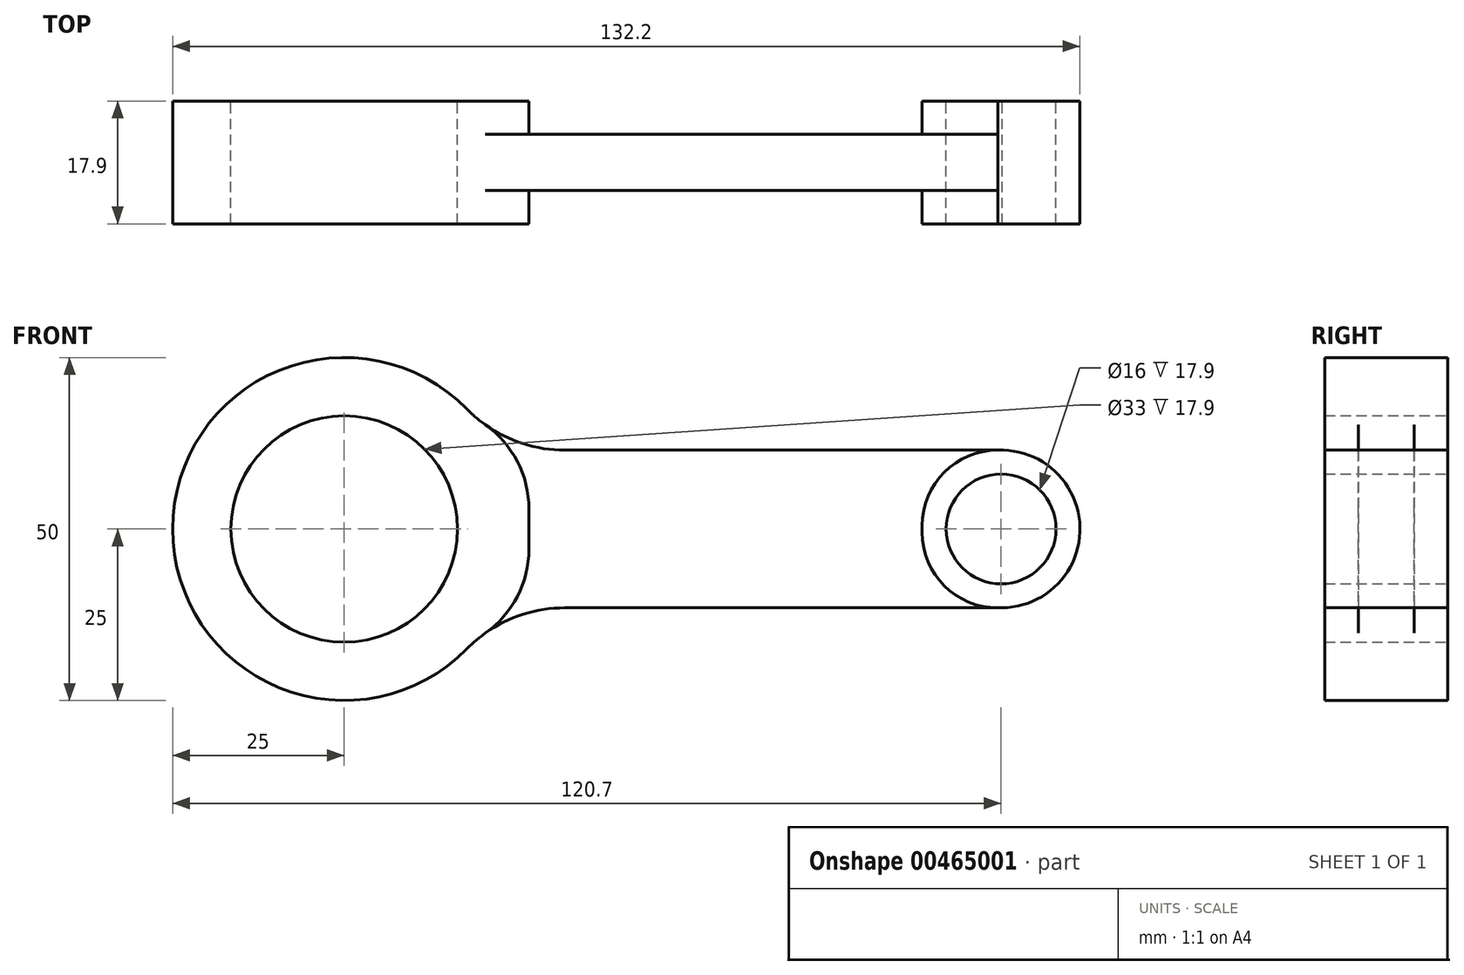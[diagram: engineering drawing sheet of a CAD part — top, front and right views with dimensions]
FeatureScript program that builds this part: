
annotation { "Feature Type Name" : "Feature", "Feature Type Description" : "" }
export const myFeature = defineFeature(function(context is Context, id is Id, definition is map)
    precondition{}
    {
        {
            var Q0;
            Q0=qCreatedBy(makeId("Front.planeOp"),FACE);
            var sketch = newSketch(context, id + "F0", { "sketchPlane" : qUnion([Q0])});
            skCircle(sketch, "E0", {"center": v(0, 0) * mm, "radius": 16.5 * mm});
            skCircle(sketch, "E1", {"center": v(95.7, 0) * mm, "radius": 8 * mm});
            skArc(sketch, "E2", {"start": v(95.55, -11.5) * mm, "mid": v(107.2, 0.15) * mm, "end": v(95.26, 11.5) * mm});
            skArc(sketch, "E3", {"start": v(17.86, 17.5) * mm, "mid": v(-25, 0) * mm, "end": v(17.85, -17.5) * mm});
            skLineSegment(sketch, "E4", {"start": v(95.26, 11.5) * mm, "end": v(32.14, 11.5) * mm});
            skLineSegment(sketch, "E5", {"start": v(95.85, -11.5) * mm, "end": v(32.14, -11.5) * mm});
            skPoint(sketch, "E6.visualSharp", {"position": v(22.2, 11.5) * mm});
            skArc(sketch, "E6.filletArc", {"start": v(17.86, 17.5) * mm, "mid": v(24.4, 13.05) * mm, "end": v(32.14, 11.5) * mm});
            skPoint(sketch, "E7.visualSharp", {"position": v(22.2, -11.5) * mm});
            skArc(sketch, "E7.filletArc", {"start": v(32.14, -11.5) * mm, "mid": v(24.4, -13.06) * mm, "end": v(17.85, -17.5) * mm});
            skSolve(sketch);
        }
        {
            var Q0;
            Q0=makeQuery(id+"F0.imprint","IMPRINT",FACE,{"disambiguationData":[TD([[makeQuery(id+"F0.imprint","IMPRINT",EDGE,{"derivedFrom":sQuery(id+"F0.wireOp",EDGE,"E0")}),-1.0]])]});
            extrude(context, id + "F1", {"entities" : qUnion([Q0]), "depth" : 17.9 * mm});
        }
        {
            var Q0;
            Q0=qCreatedBy(makeId("Top.planeOp"),FACE);
            var sketch = newSketch(context, id + "F2", { "sketchPlane" : qUnion([Q0])});
            skLineSegment(sketch, "E8", {"start": v(-25, -17.9) * mm, "end": v(-25, 0) * mm, "construction": true});
            skLineSegment(sketch, "E9", {"start": v(107.2, 0) * mm, "end": v(107.2, -17.9) * mm, "construction": true});
            skLineSegment(sketch, "E10", {"start": v(-25, -8.95) * mm, "end": v(107.2, -8.95) * mm, "construction": true});
            skLineSegment(sketch, "E11.bottom", {"start": v(26.9, 6.17) * mm, "end": v(84.2, 6.17) * mm});
            skLineSegment(sketch, "E11.top", {"start": v(26.9, -4.88) * mm, "end": v(84.2, -4.88) * mm});
            skLineSegment(sketch, "E11.left", {"start": v(26.9, 6.17) * mm, "end": v(26.9, -4.88) * mm});
            skLineSegment(sketch, "E11.right", {"start": v(84.2, 6.17) * mm, "end": v(84.2, -4.88) * mm});
            skLineSegment(sketch, "E12.bottom", {"start": v(26.9, -23.79) * mm, "end": v(84.2, -23.79) * mm});
            skLineSegment(sketch, "E12.top", {"start": v(26.9, -13.03) * mm, "end": v(84.2, -13.03) * mm});
            skLineSegment(sketch, "E12.left", {"start": v(26.9, -23.79) * mm, "end": v(26.9, -13.03) * mm});
            skLineSegment(sketch, "E12.right", {"start": v(84.2, -23.79) * mm, "end": v(84.2, -13.03) * mm});
            skSolve(sketch);
        }
        {
            var Q0;
            Q0 = qSketchRegion(id + "F2", true);
            extrude(context, id + "F3", {"entities" : qUnion([Q0]), "operationType" : NewBodyOperationType.REMOVE, "endBound" : BoundingType.THROUGH_ALL, "oppositeDirection" : true, "depth" : 25 * mm, "hasSecondDirection" : true, "secondDirectionBound" : SecondDirectionBoundingType.THROUGH_ALL, "secondDirectionOppositeDirection" : false, "secondDirectionDepth" : 25 * mm});
        }
        {
            var Q0;
            Q0=makeQuery(id+"F3.boolean.opBoolean","INTERSECT",EDGE,{"derivedFrom":[makeQuery(id+"F1.opExtrude","SWEPT_FACE",FACE,{"disambiguationData":[OSD([sQuery(id+"F0.wireOp",EDGE,"E5")])]}),makeQuery(id+"F3.opExtrude","SWEPT_FACE",FACE,{"disambiguationData":[OSD([sQuery(id+"F2.wireOp",EDGE,"E11.right")])]})]});
            fillet(context, id + "F4", {"entities" : qUnion([Q0]), "radius" : 11 * mm, "tangentPropagation" : true, "allowEdgeOverflow" : false});
        }
        {
            var Q0;
            Q0=makeQuery(id+"F3.boolean.opBoolean","INTERSECT",EDGE,{"derivedFrom":[makeQuery(id+"F1.opExtrude","SWEPT_FACE",FACE,{"disambiguationData":[OSD([sQuery(id+"F0.wireOp",EDGE,"E4")])]}),makeQuery(id+"F3.opExtrude","SWEPT_FACE",FACE,{"disambiguationData":[OSD([sQuery(id+"F2.wireOp",EDGE,"E11.right")])]})]});
            fillet(context, id + "F5", {"entities" : qUnion([Q0]), "radius" : 11 * mm, "tangentPropagation" : true, "allowEdgeOverflow" : false});
        }
        {
            var Q0;
            Q0=makeQuery(id+"F3.boolean.opBoolean","INTERSECT",EDGE,{"derivedFrom":[makeQuery(id+"F1.opExtrude","SWEPT_FACE",FACE,{"disambiguationData":[OSD([sQuery(id+"F0.wireOp",EDGE,"E5")])]}),makeQuery(id+"F3.opExtrude","SWEPT_FACE",FACE,{"disambiguationData":[OSD([sQuery(id+"F2.wireOp",EDGE,"E12.right")])]})]});
            var Q1;
            Q1=makeQuery(id+"F3.boolean.opBoolean","INTERSECT",EDGE,{"derivedFrom":[makeQuery(id+"F1.opExtrude","SWEPT_FACE",FACE,{"disambiguationData":[OSD([sQuery(id+"F0.wireOp",EDGE,"E4")])]}),makeQuery(id+"F3.opExtrude","SWEPT_FACE",FACE,{"disambiguationData":[OSD([sQuery(id+"F2.wireOp",EDGE,"E12.right")])]})]});
            fillet(context, id + "F6", {"entities" : qUnion([Q0, Q1]), "radius" : 11 * mm, "tangentPropagation" : true, "allowEdgeOverflow" : false});
        }
        {
            var Q0;
            Q0=makeQuery(id+"F3.boolean.opBoolean","INTERSECT",EDGE,{"derivedFrom":[makeQuery(id+"F1.opExtrude","SWEPT_FACE",FACE,{"disambiguationData":[OSD([sQuery(id+"F0.wireOp",EDGE,"E7.filletArc")])]}),makeQuery(id+"F3.opExtrude","SWEPT_FACE",FACE,{"disambiguationData":[OSD([sQuery(id+"F2.wireOp",EDGE,"E11.left")])]})]});
            var Q1;
            Q1=makeQuery(id+"F3.boolean.opBoolean","INTERSECT",EDGE,{"derivedFrom":[makeQuery(id+"F1.opExtrude","SWEPT_FACE",FACE,{"disambiguationData":[OSD([sQuery(id+"F0.wireOp",EDGE,"E6.filletArc")])]}),makeQuery(id+"F3.opExtrude","SWEPT_FACE",FACE,{"disambiguationData":[OSD([sQuery(id+"F2.wireOp",EDGE,"E11.left")])]})]});
            var Q2;
            Q2=makeQuery(id+"F3.boolean.opBoolean","INTERSECT",EDGE,{"derivedFrom":[makeQuery(id+"F1.opExtrude","SWEPT_FACE",FACE,{"disambiguationData":[OSD([sQuery(id+"F0.wireOp",EDGE,"E7.filletArc")])]}),makeQuery(id+"F3.opExtrude","SWEPT_FACE",FACE,{"disambiguationData":[OSD([sQuery(id+"F2.wireOp",EDGE,"E12.left")])]})]});
            var Q3;
            Q3=makeQuery(id+"F3.boolean.opBoolean","INTERSECT",EDGE,{"derivedFrom":[makeQuery(id+"F1.opExtrude","SWEPT_FACE",FACE,{"disambiguationData":[OSD([sQuery(id+"F0.wireOp",EDGE,"E6.filletArc")])]}),makeQuery(id+"F3.opExtrude","SWEPT_FACE",FACE,{"disambiguationData":[OSD([sQuery(id+"F2.wireOp",EDGE,"E12.left")])]})]});
            fillet(context, id + "F7", {"entities" : qUnion([Q0, Q1, Q2, Q3]), "radius" : 15 * mm, "tangentPropagation" : true, "allowEdgeOverflow" : false});
        }
    });
